# Revit family: Locker_Benches-Salsbury_Industries-Aluminum_77770_Series
name_source: partatom
category: Specialty Equipment
units: mm (PartAtom-declared; Revit-internal decimal feet)

## family parameters
Always vertical = Yes
Classification Number = 23.40.00.00
Cut with Voids When Loaded = No
Enable Cutting in Views = No
Maintain Annotation Orientation = No
Part Type = Normal
Room Calculation Point = No
Round Connector Dimension = Use Diameter
Shared = No
Work Plane-Based = No

## types (6) — shared parameters
Assembly Code = C1030310
Depth = 9.625 "
Height = 18 "
Manufacturer = Salsbury Industries
MasterFormat Number = 10 51 53
MasterFormat Title = Locker Room Benches
OmniClass 23 Number = 23.40.00.00
OmniClass 23 Title = Equipment and Furnishings
Pedestal Offset = 6 "
Primary Material = Aluminum - Salsbury Finish - Aluminum
Secondary Material = Paint - Salsbury Finish - Aluminum
Type Comments = Aluminum Locker Bench
URL = www.lockers.com
Version = 1.0 (11/16/18)
zero-valued in all types: Default Elevation

## per-type parameters (varying)
| type | Description | Width |
| 77776 | 72 Inches Wide | 72.25 " |
| 77777 | 84 Inches Wide | 84.25 " |
| 77778 | 96 Inches Wide | 96.25 " |
| 77775 | 60 Inches Wide | 60.25 " |
| 77774 | 48 Inches Wide | 48.25 " |
| 77773 | 36 Inches Wide | 36.25 " |

note: column(s) folded — value = type name in every type: Model

## geometry (parser evidence)
native form markers: Sweep x3
no freeform markers — native parametric forms only
